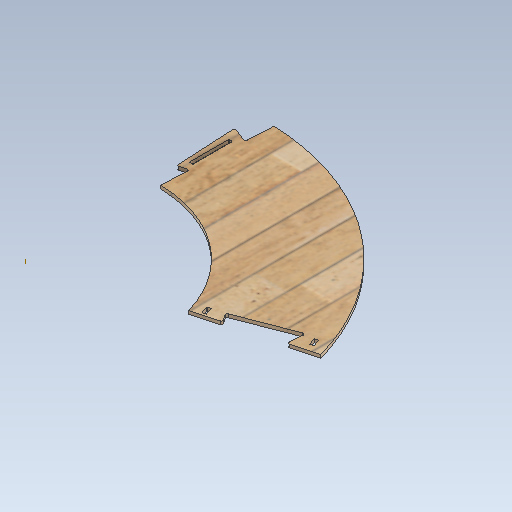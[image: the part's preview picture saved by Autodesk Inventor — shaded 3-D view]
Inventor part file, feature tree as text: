
AUTODESK INVENTOR PART (.ipt)
format: ipt  version: 2020 (Build 240168000, 168)  size: 468,992 bytes
history: native  units: mm
features: extrude x5, sketch x4, pattern_circular x3, mirror x2
ambient origin geometry x8: Origin, YZ Plane, XZ Plane, XY Plane, X Axis, Y Axis, Z Axis, Center Point
bodies: Body1 (feature_tree)
feature tree (14):
  extrude  "Extrusion3"  Depth=6.5mm
  extrude  "Extrusion4"  Depth=2.666667mm
  sketch  "Sketch3"  dims[d24=2.666667mm d25=2.666667mm]
  sketch  "Sketch5"  dims[d32=1.333333mm d33=1.333333mm]
  extrude  "Extrusion7"  Depth=1.333333mm
  pattern_circular  "Circular Pattern2"  [2 undecoded]
  pattern_circular  "Circular Pattern3"  [2 undecoded]
  mirror  "Mirror3"
  extrude  "Extrusion10"  Depth=70.0mm
  mirror  "Mirror4"
  pattern_circular  "Circular Pattern4"  [2 undecoded]
  extrude  "Extrusion11"  Depth=2.666667mm
  sketch  "Sketch2"  dims[d15=6.0mm d16=0.0mm d21=6.5mm]
  sketch  "Sketch6"  dims[d38=0.0mm d39=0.0mm d40=3.25mm d52=4.363323mm d60=0.872665mm d61=12.566371mm d62=13.439035mm d63=2.666667mm d64=0.523599mm d66=0.523599mm d67=2.666667mm d68=2.666667mm d70=12.566371mm d71=12.566371mm d84=467.42mm d85=850.0mm d86=658.71mm d87=150.07mm d88=425.0mm d89=4.363323mm d90=1.919862mm d91=1.919862mm d104=6.5mm d105=12.0mm d108=1.333333mm d109=1.333333mm d110=1.333333mm d111=1.333333mm d112=0.0mm d113=0.0mm d114=0.0mm d145=20.0mm d146=12.566371mm d149=145.0mm d150=90.0deg d151=90.0deg d152=90.0deg d153=90.0deg d154=20.0mm d155=25.132741mm d157=10.0mm d158=0.0mm d162=70.0mm d163=294.355mm d165=3.25mm d174=20.0mm d175=25.132741mm d177=0.0mm d178=0.0mm d176=0.5mm]
note: 6 required parameter values undecoded (feature->parameter linkage not recoverable at this tier; creation-order binding heuristic only, values carry confidence <= 0.55)
